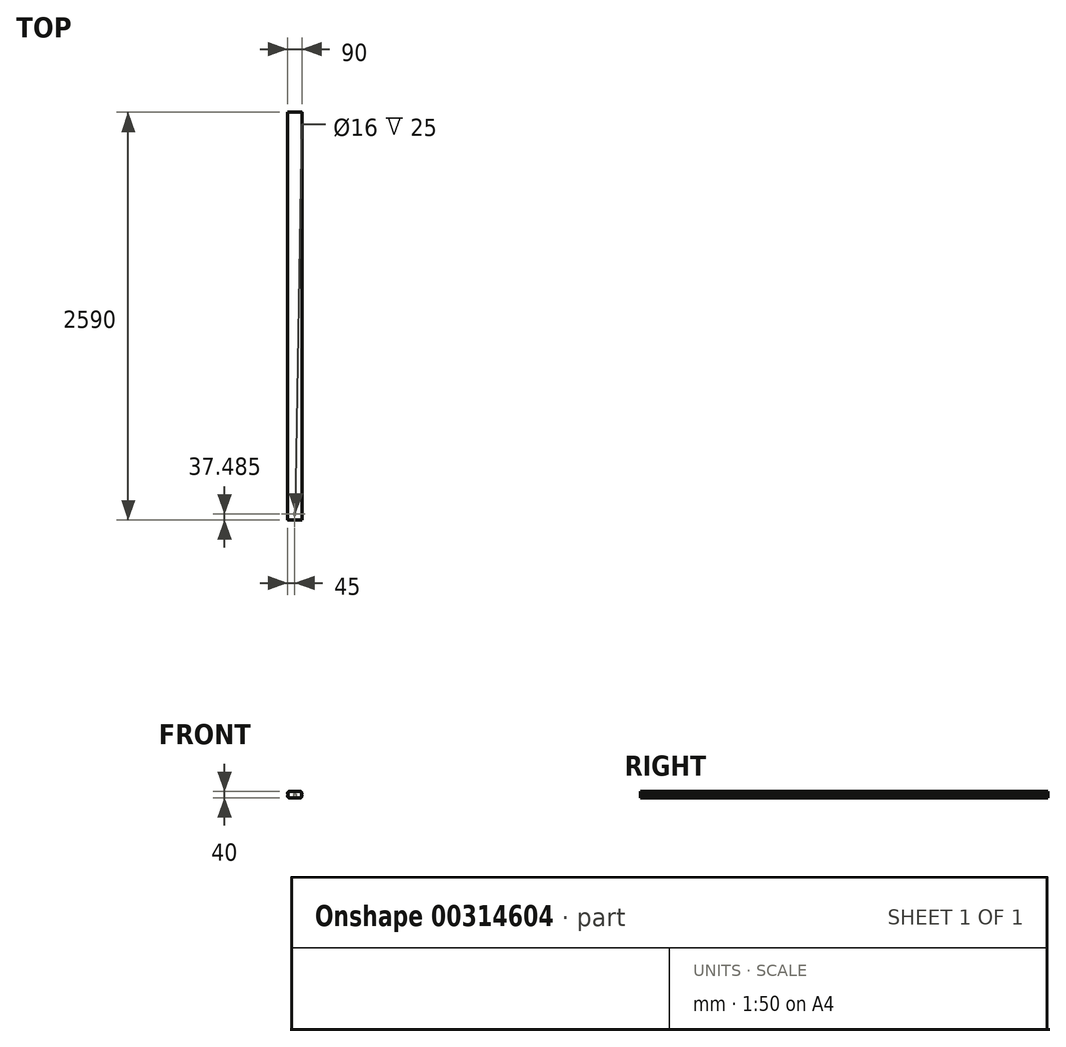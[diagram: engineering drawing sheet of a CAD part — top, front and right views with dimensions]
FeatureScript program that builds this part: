
annotation { "Feature Type Name" : "Feature", "Feature Type Description" : "" }
export const myFeature = defineFeature(function(context is Context, id is Id, definition is map)
    precondition{}
    {
        {
            var Q0;
            Q0=qCreatedBy(makeId("Front.planeOp"),FACE);
            var sketch = newSketch(context, id + "F0", { "sketchPlane" : qUnion([Q0])});
            skLineSegment(sketch, "E0.bottom", {"start": v(35, -20) * mm, "end": v(-35, -20) * mm});
            skLineSegment(sketch, "E0.top", {"start": v(35, 20) * mm, "end": v(-35, 20) * mm});
            skPoint(sketch, "E0.middle", {"position": v(0, 0) * mm});
            skPoint(sketch, "E1.visualSharp", {"position": v(-45, 20) * mm});
            skArc(sketch, "E1.filletArc", {"start": v(-35, 20) * mm, "mid": v(-42.07, 17.07) * mm, "end": v(-45, 10) * mm});
            skPoint(sketch, "E2.visualSharp", {"position": v(-45, -20) * mm});
            skArc(sketch, "E2.filletArc", {"start": v(-45, -10) * mm, "mid": v(-42.07, -17.07) * mm, "end": v(-35, -20) * mm});
            skPoint(sketch, "E3.visualSharp", {"position": v(45, -20) * mm});
            skArc(sketch, "E3.filletArc", {"start": v(35, -20) * mm, "mid": v(42.07, -17.07) * mm, "end": v(45, -10) * mm});
            skPoint(sketch, "E4.visualSharp", {"position": v(45, 20) * mm});
            skArc(sketch, "E4.filletArc", {"start": v(45, 10) * mm, "mid": v(42.07, 17.07) * mm, "end": v(35, 20) * mm});
            skLineSegment(sketch, "E5", {"start": v(-45, 10) * mm, "end": v(-42.9, 2.8) * mm});
            skLineSegment(sketch, "E6", {"start": v(-42.9, -2.8) * mm, "end": v(-45, -10) * mm});
            skPoint(sketch, "E7.visualSharp", {"position": v(-42.1, 0) * mm});
            skArc(sketch, "E7.filletArc", {"start": v(-42.9, -2.8) * mm, "mid": v(-42.5, 0) * mm, "end": v(-42.9, 2.8) * mm});
            skArc(sketch, "E8.MirrorCS", {"start": v(35, 20) * mm, "mid": v(42.07, 17.07) * mm, "end": v(45, 10) * mm});
            skLineSegment(sketch, "E9.MirrorCS", {"start": v(45, 10) * mm, "end": v(42.9, 2.8) * mm});
            skArc(sketch, "E10.MirrorCS", {"start": v(42.9, -2.8) * mm, "mid": v(42.5, 0) * mm, "end": v(42.9, 2.8) * mm});
            skLineSegment(sketch, "E11.MirrorCS", {"start": v(42.9, -2.8) * mm, "end": v(45, -10) * mm});
            skArc(sketch, "E12.MirrorCS", {"start": v(45, -10) * mm, "mid": v(42.07, -17.07) * mm, "end": v(35, -20) * mm});
            skSolve(sketch);
        }
        {
            var Q0;
            Q0=makeQuery(id+"F0.imprint","IMPRINT",FACE,{"disambiguationData":[TD([[makeQuery(id+"F0.imprint","IMPRINT",EDGE,{"derivedFrom":sQuery(id+"F0.wireOp",EDGE,"E0.bottom")}),-1.0]])]});
            extrude(context, id + "F1", {"entities" : qUnion([Q0]), "depth" : 2590 * mm});
        }
        {
            var Q0;
            Q0=makeQuery(id+"F1.opExtrude","SWEPT_FACE",FACE,{"disambiguationData":[OSD([sQuery(id+"F0.wireOp",EDGE,"E0.bottom")])]});
            var sketch = newSketch(context, id + "F2", { "sketchPlane" : qUnion([Q0])});
            skCircle(sketch, "E13", {"center": v(0, 2552.52) * mm, "radius": 8 * mm});
            skPoint(sketch, "E13.centerSnap0", {"position": v(0, 2590) * mm});
            skSolve(sketch);
        }
        {
            var Q0;
            Q0=makeQuery(id+"F2.imprint","IMPRINT",FACE,{"disambiguationData":[TD([[makeQuery(id+"F2.imprint","IMPRINT",EDGE,{"derivedFrom":sQuery(id+"F2.wireOp",EDGE,"E13")}),1.0]])]});
            extrude(context, id + "F3", {"entities" : qUnion([Q0]), "operationType" : NewBodyOperationType.REMOVE, "depth" : -25 * mm});
        }
    });
